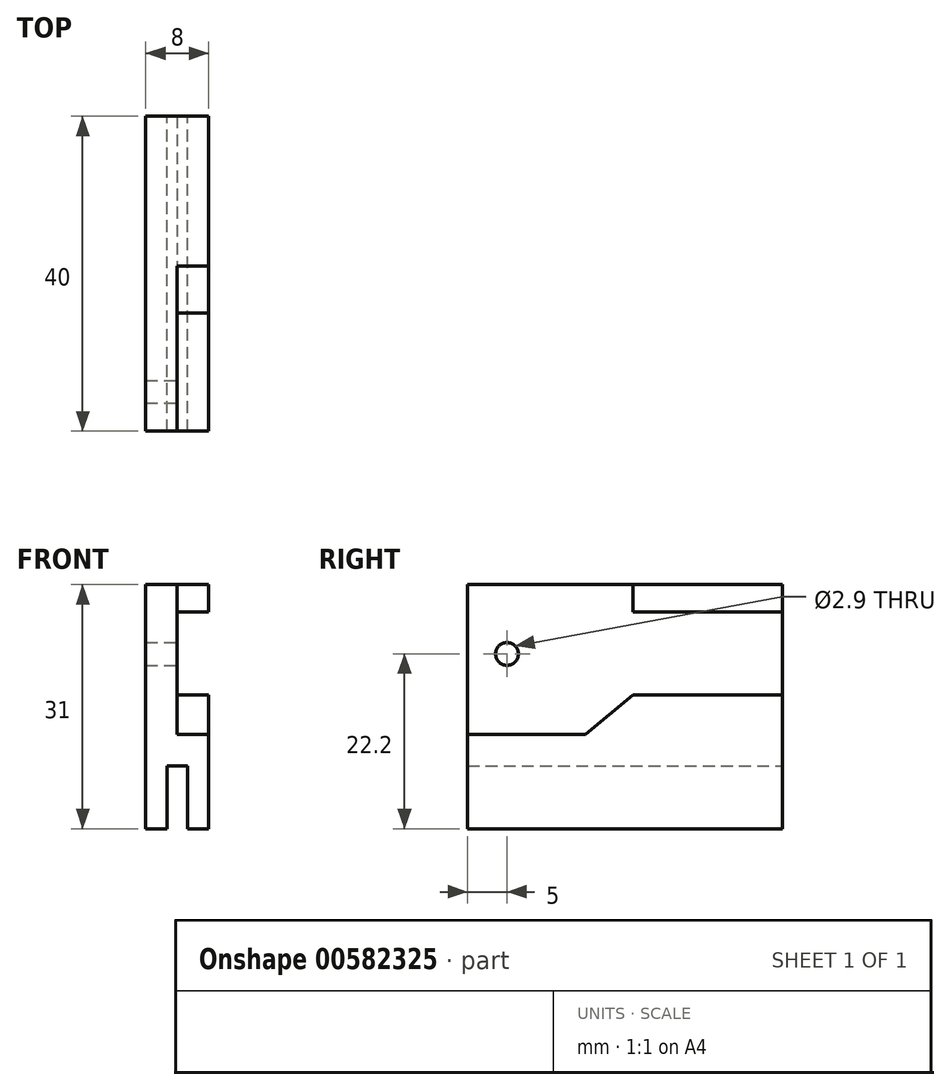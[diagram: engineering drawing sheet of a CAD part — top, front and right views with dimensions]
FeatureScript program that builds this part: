
annotation { "Feature Type Name" : "Feature", "Feature Type Description" : "" }
export const myFeature = defineFeature(function(context is Context, id is Id, definition is map)
    precondition{}
    {
        {
            var Q0;
            Q0=qCreatedBy(makeId("Front.planeOp"),FACE);
            var sketch = newSketch(context, id + "F0", { "sketchPlane" : qUnion([Q0])});
            skLineSegment(sketch, "E0.bottom", {"start": v(4, 15.5) * mm, "end": v(-4, 15.5) * mm});
            skLineSegment(sketch, "E0.top", {"start": v(4, -15.5) * mm, "end": v(1.3, -15.5) * mm});
            skLineSegment(sketch, "E0.left", {"start": v(4, 15.5) * mm, "end": v(4, -15.5) * mm});
            skLineSegment(sketch, "E0.right", {"start": v(-4, 15.5) * mm, "end": v(-4, -15.5) * mm});
            skPoint(sketch, "E0.middle", {"position": v(0, 0) * mm});
            skLineSegment(sketch, "E1", {"start": v(-1.3, -15.5) * mm, "end": v(-1.3, -7.5) * mm});
            skLineSegment(sketch, "E2", {"start": v(-1.3, -7.5) * mm, "end": v(1.3, -7.5) * mm});
            skLineSegment(sketch, "E3", {"start": v(1.3, -7.5) * mm, "end": v(1.3, -15.5) * mm});
            skLineSegment(sketch, "E4.trimOffspring", {"start": v(-1.3, -15.5) * mm, "end": v(-4, -15.5) * mm});
            skSolve(sketch);
        }
        {
            var Q0;
            Q0 = qSketchRegion(id + "F0", true);
            extrude(context, id + "F1", {"entities" : qUnion([Q0]), "endBound" : BoundingType.SYMMETRIC, "depth" : 40 * mm, "offsetDistance" : 25 * mm});
        }
        {
            var Q0;
            Q0=makeQuery(id+"F1.opExtrude","SWEPT_FACE",FACE,{"disambiguationData":[OSD([sQuery(id+"F0.wireOp",EDGE,"E0.left")])]});
            var sketch = newSketch(context, id + "F2", { "sketchPlane" : qUnion([Q0])});
            skLineSegment(sketch, "E5", {"start": v(-20, -3.5) * mm, "end": v(-5, -3.5) * mm});
            skLineSegment(sketch, "E6", {"start": v(-5, -3.5) * mm, "end": v(1, 1.5) * mm});
            skLineSegment(sketch, "E7", {"start": v(1, 1.5) * mm, "end": v(20, 1.5) * mm});
            skLineSegment(sketch, "E8", {"start": v(20, 1.5) * mm, "end": v(20, 12) * mm});
            skLineSegment(sketch, "E9", {"start": v(1, 15.5) * mm, "end": v(-20, 15.5) * mm});
            skLineSegment(sketch, "E10", {"start": v(-20, 15.5) * mm, "end": v(-20, -3.5) * mm});
            skLineSegment(sketch, "E11", {"start": v(1, 15.5) * mm, "end": v(1, 12) * mm});
            skPoint(sketch, "E11.startSnap0", {"position": v(0, 15.5) * mm});
            skLineSegment(sketch, "E12", {"start": v(1, 12) * mm, "end": v(20, 12) * mm});
            skSolve(sketch);
        }
        {
            var Q0;
            Q0 = qSketchRegion(id + "F2", true);
            var Q1;
            Q1=qCreatedBy(makeId("Right.planeOp"),FACE);
            extrude(context, id + "F3", {"entities" : qUnion([Q0]), "operationType" : NewBodyOperationType.REMOVE, "endBound" : BoundingType.UP_TO_SURFACE, "oppositeDirection" : true, "depth" : 4 * mm, "endBoundEntityFace" : qUnion([Q1]), "offsetDistance" : 25 * mm});
        }
        {
            var Q0;
            Q0=makeQuery(id+"F3.boolean.opBoolean","COPY",FACE,{"derivedFrom":makeQuery(id+"F3.opExtrude","CAP_FACE",FACE,{"disambiguationData":[OSD([sQuery(id+"F2.wireOp",EDGE,"E5"),sQuery(id+"F2.wireOp",EDGE,"E6"),sQuery(id+"F2.wireOp",EDGE,"E7"),sQuery(id+"F2.wireOp",EDGE,"E8"),sQuery(id+"F2.wireOp",EDGE,"E9"),sQuery(id+"F2.wireOp",EDGE,"E10"),sQuery(id+"F2.wireOp",EDGE,"E11"),sQuery(id+"F2.wireOp",EDGE,"E12")])],"isStart":false})});
            var sketch = newSketch(context, id + "F4", { "sketchPlane" : qUnion([Q0])});
            skCircle(sketch, "E13", {"center": v(-15, 6.7) * mm, "radius": 1.45 * mm});
            skSolve(sketch);
        }
        {
            var Q0;
            Q0 = qSketchRegion(id + "F4", true);
            extrude(context, id + "F5", {"entities" : qUnion([Q0]), "operationType" : NewBodyOperationType.REMOVE, "oppositeDirection" : true, "depth" : 25 * mm, "offsetDistance" : 25 * mm});
        }
    });
